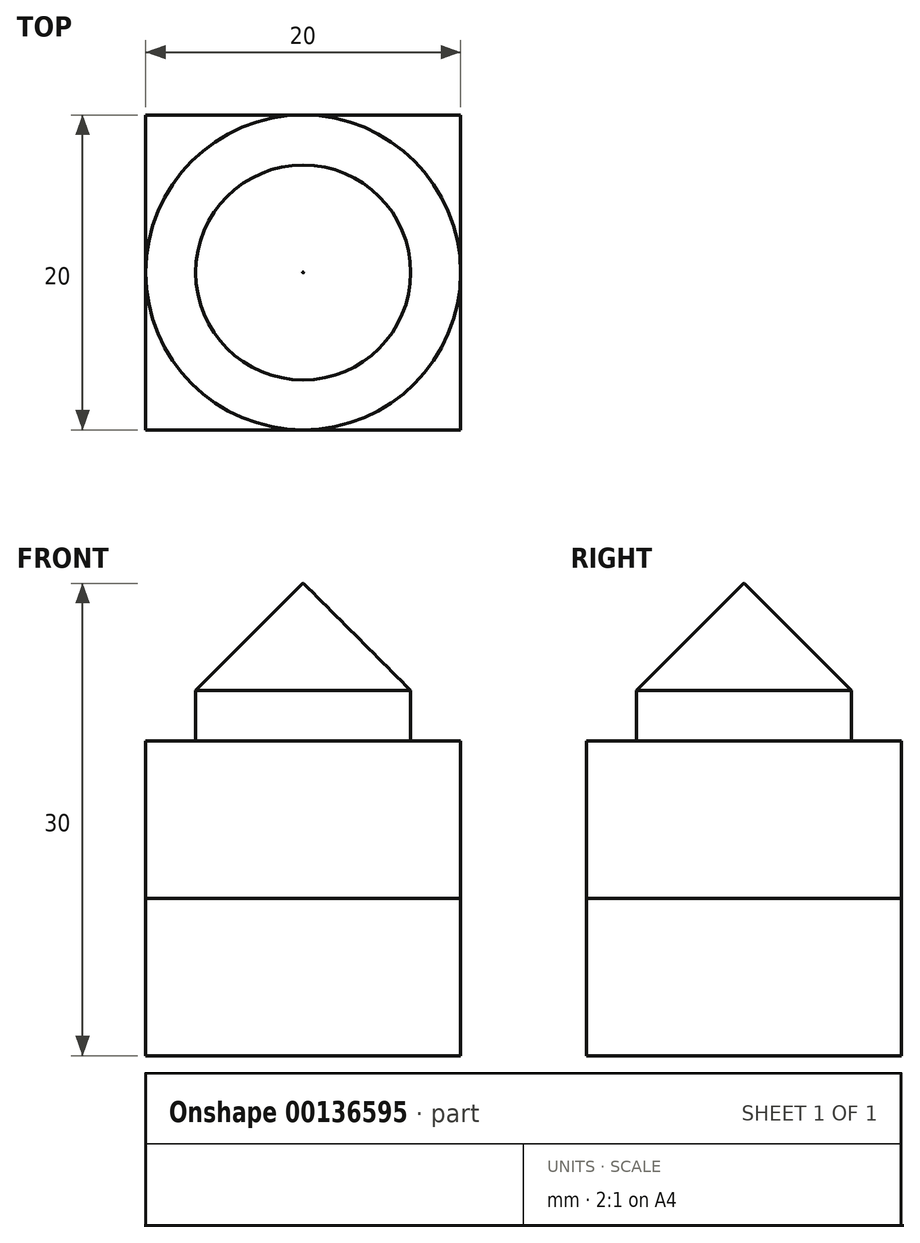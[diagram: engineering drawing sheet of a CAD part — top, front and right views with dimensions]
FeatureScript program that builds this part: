
annotation { "Feature Type Name" : "Feature", "Feature Type Description" : "" }
export const myFeature = defineFeature(function(context is Context, id is Id, definition is map)
    precondition{}
    {
        {
            var Q0;
            Q0=qCreatedBy(makeId("Top.planeOp"),FACE);
            var sketch = newSketch(context, id + "F0", { "sketchPlane" : qUnion([Q0])});
            skLineSegment(sketch, "E0.bottom", {"start": v(-10, 10) * mm, "end": v(10, 10) * mm});
            skLineSegment(sketch, "E0.top", {"start": v(-10, -10) * mm, "end": v(10, -10) * mm});
            skLineSegment(sketch, "E0.left", {"start": v(-10, 10) * mm, "end": v(-10, -10) * mm});
            skLineSegment(sketch, "E0.right", {"start": v(10, 10) * mm, "end": v(10, -10) * mm});
            skPoint(sketch, "E0.middle", {"position": v(0, 0) * mm});
            skSolve(sketch);
        }
        {
            var Q0;
            Q0 = qSketchRegion(id + "F0", true);
            extrude(context, id + "F1", {"entities" : qUnion([Q0]), "depth" : 10 * mm});
        }
        {
            var Q0;
            Q0=makeQuery(id+"F1.opExtrude","CAP_FACE",FACE,{"disambiguationData":[OSD([sQuery(id+"F0.wireOp",EDGE,"E0.bottom"),sQuery(id+"F0.wireOp",EDGE,"E0.top"),sQuery(id+"F0.wireOp",EDGE,"E0.left"),sQuery(id+"F0.wireOp",EDGE,"E0.right")])],"isStart":false});
            var sketch = newSketch(context, id + "F2", { "sketchPlane" : qUnion([Q0])});
            skCircle(sketch, "E1", {"center": v(0, 0) * mm, "radius": 10 * mm});
            skSolve(sketch);
        }
        {
            var Q0;
            Q0 = qSketchRegion(id + "F2", true);
            extrude(context, id + "F3", {"entities" : qUnion([Q0]), "operationType" : NewBodyOperationType.ADD, "depth" : 10 * mm});
        }
        {
            var Q0;
            Q0=makeQuery(id+"F3.opExtrude","CAP_FACE",FACE,{"disambiguationData":[OSD([sQuery(id+"F2.wireOp",EDGE,"E1")])],"isStart":false});
            var sketch = newSketch(context, id + "F4", { "sketchPlane" : qUnion([Q0])});
            skCircle(sketch, "E2", {"center": v(0, 0) * mm, "radius": 6.83 * mm});
            skSolve(sketch);
        }
        {
            var Q0;
            Q0 = qSketchRegion(id + "F4", true);
            extrude(context, id + "F5", {"entities" : qUnion([Q0]), "operationType" : NewBodyOperationType.ADD, "depth" : 10 * mm});
        }
        {
            var Q0;
            Q0=makeQuery(id+"F5.opExtrude","CAP_EDGE",EDGE,{"disambiguationData":[OSD([sQuery(id+"F4.wireOp",EDGE,"E2")])],"isStart":false});
            chamfer(context, id + "F6", {"entities" : qUnion([Q0]), "width" : 6.8 * mm, "tangentPropagation" : true});
        }
    });
